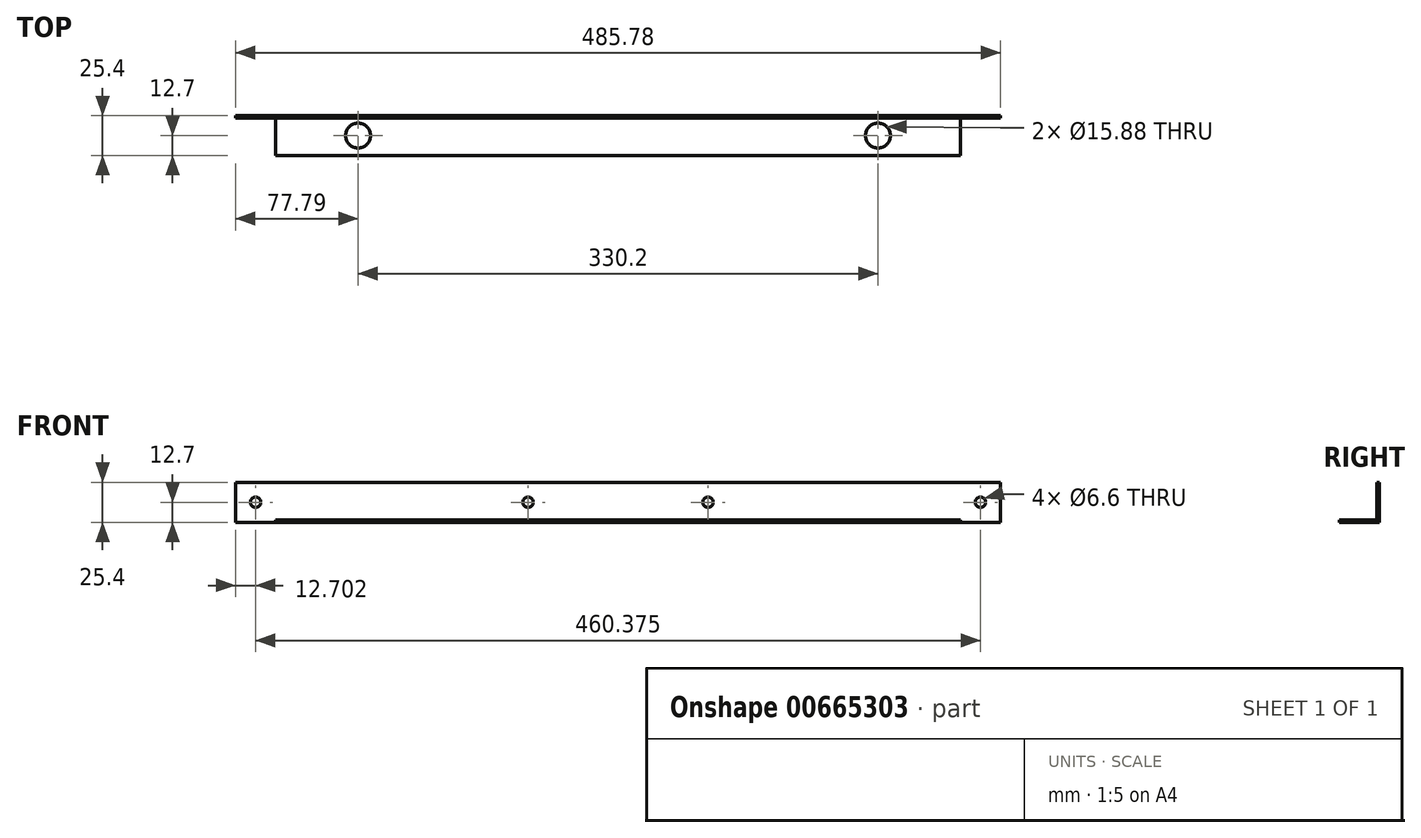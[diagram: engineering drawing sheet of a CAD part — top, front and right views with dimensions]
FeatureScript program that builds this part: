
annotation { "Feature Type Name" : "Feature", "Feature Type Description" : "" }
export const myFeature = defineFeature(function(context is Context, id is Id, definition is map)
    precondition{}
    {
        {
            var Q0;
            Q0=qCreatedBy(makeId("Right.planeOp"),FACE);
            var sketch = newSketch(context, id + "F0", { "sketchPlane" : qUnion([Q0])});
            skLineSegment(sketch, "E0", {"start": v(0, 25.4) * mm, "end": v(0, 0) * mm});
            skLineSegment(sketch, "E1", {"start": v(0, 0) * mm, "end": v(-25.4, 0) * mm});
            skLineSegment(sketch, "E2", {"start": v(-25.4, 0) * mm, "end": v(-25.4, 1.59) * mm});
            skLineSegment(sketch, "E3", {"start": v(-25.4, 1.59) * mm, "end": v(-1.59, 1.59) * mm});
            skLineSegment(sketch, "E4", {"start": v(-1.59, 1.59) * mm, "end": v(-1.59, 25.4) * mm});
            skLineSegment(sketch, "E5", {"start": v(0, 25.4) * mm, "end": v(-1.59, 25.4) * mm});
            skSolve(sketch);
        }
        {
            var Q0;
            Q0=makeQuery(id+"F0.imprint","IMPRINT",FACE,{"disambiguationData":[TD([[makeQuery(id+"F0.imprint","IMPRINT",EDGE,{"derivedFrom":sQuery(id+"F0.wireOp",EDGE,"E0")}),-1.0]])]});
            extrude(context, id + "F1", {"entities" : qUnion([Q0]), "depth" : 485.77 * mm, "offsetDistance" : 25.4 * mm, "symmetric" : true});
        }
        {
            var Q0;
            Q0=makeQuery(id+"F1.opExtrude","SWEPT_FACE",FACE,{"disambiguationData":[OSD([sQuery(id+"F0.wireOp",EDGE,"E1")])]});
            var sketch = newSketch(context, id + "F2", { "sketchPlane" : qUnion([Q0])});
            skCircle(sketch, "E6", {"center": v(-165.1, 12.7) * mm, "radius": 7.94 * mm});
            skCircle(sketch, "E7", {"center": v(165.1, 12.7) * mm, "radius": 7.94 * mm});
            skLineSegment(sketch, "E8", {"start": v(0, 0) * mm, "end": v(0, 25.4) * mm, "construction": true});
            skLineSegment(sketch, "E9", {"start": v(-165.1, 12.7) * mm, "end": v(165.1, 12.7) * mm, "construction": true});
            skPoint(sketch, "E10", {"position": v(0, 12.7) * mm});
            skLineSegment(sketch, "E11.0.0", {"start": v(-242.89, 1.59) * mm, "end": v(-242.89, 25.4) * mm});
            skLineSegment(sketch, "E11.0.1", {"start": v(-242.89, 25.4) * mm, "end": v(242.89, 25.4) * mm});
            skLineSegment(sketch, "E11.0.2", {"start": v(242.89, 25.4) * mm, "end": v(242.89, 1.59) * mm});
            skLineSegment(sketch, "E11.0.3", {"start": v(242.89, 1.59) * mm, "end": v(-242.89, 1.59) * mm});
            skLineSegment(sketch, "E12", {"start": v(-217.49, 1.59) * mm, "end": v(-217.49, 25.4) * mm});
            skLineSegment(sketch, "E13.MirrorCS", {"start": v(217.49, 1.59) * mm, "end": v(217.49, 25.4) * mm});
            skSolve(sketch);
        }
        {
            var Q0;
            Q0=makeQuery(id+"F1.opExtrude","SWEPT_FACE",FACE,{"disambiguationData":[OSD([sQuery(id+"F0.wireOp",EDGE,"E4")])]});
            var sketch = newSketch(context, id + "F3", { "sketchPlane" : qUnion([Q0])});
            skLineSegment(sketch, "E14", {"start": v(0, 0) * mm, "end": v(0, 25.4) * mm, "construction": true});
            skLineSegment(sketch, "E15", {"start": v(230.19, 12.7) * mm, "end": v(-230.19, 12.7) * mm, "construction": true});
            skPoint(sketch, "E15.startSnap0", {"position": v(0, 12.7) * mm});
            skCircle(sketch, "E16", {"center": v(-230.19, 12.7) * mm, "radius": 3.3 * mm});
            skCircle(sketch, "E17", {"center": v(230.19, 12.7) * mm, "radius": 3.3 * mm});
            skLineSegment(sketch, "E18", {"start": v(57.15, 12.7) * mm, "end": v(-57.15, 12.7) * mm, "construction": true});
            skCircle(sketch, "E19", {"center": v(-57.15, 12.7) * mm, "radius": 3.3 * mm});
            skCircle(sketch, "E20", {"center": v(57.15, 12.7) * mm, "radius": 3.3 * mm});
            skSolve(sketch);
        }
        {
            var Q0;
            Q0=makeQuery(id+"F2.imprint","IMPRINT",FACE,{"disambiguationData":[TD([[makeQuery(id+"F2.imprint","IMPRINT",EDGE,{"derivedFrom":sQuery(id+"F2.wireOp",EDGE,"E6")}),1.0]])]});
            var Q1;
            Q1=makeQuery(id+"F2.imprint","IMPRINT",FACE,{"disambiguationData":[TD([[makeQuery(id+"F2.imprint","IMPRINT",EDGE,{"derivedFrom":sQuery(id+"F2.wireOp",EDGE,"E7")}),1.0]])]});
            var Q2;
            {var subQ0=sQuery(id+"F2.wireOp",EDGE,"E11.0.0");Q2=makeQuery(id+"F2.imprint","IMPRINT",FACE,{"disambiguationData":[TD([[makeQuery(id+"F2.imprint","IMPRINT",EDGE,{"derivedFrom":subQ0}),-1.0]])]});}
            var Q3;
            {var subQ0=sQuery(id+"F2.wireOp",EDGE,"E11.0.2");Q3=makeQuery(id+"F2.imprint","IMPRINT",FACE,{"disambiguationData":[TD([[makeQuery(id+"F2.imprint","IMPRINT",EDGE,{"derivedFrom":subQ0}),1.0]])]});}
            extrude(context, id + "F4", {"entities" : qUnion([Q0, Q1, Q2, Q3]), "operationType" : NewBodyOperationType.REMOVE, "oppositeDirection" : true, "depth" : 25.4 * mm, "offsetDistance" : 25.4 * mm});
        }
        {
            var Q0;
            Q0=makeQuery(id+"F3.imprint","IMPRINT",FACE,{"disambiguationData":[TD([[makeQuery(id+"F3.imprint","IMPRINT",EDGE,{"derivedFrom":sQuery(id+"F3.wireOp",EDGE,"E16")}),1.0]])]});
            var Q1;
            Q1=makeQuery(id+"F3.imprint","IMPRINT",FACE,{"disambiguationData":[TD([[makeQuery(id+"F3.imprint","IMPRINT",EDGE,{"derivedFrom":sQuery(id+"F3.wireOp",EDGE,"E17")}),1.0]])]});
            var Q2;
            Q2=makeQuery(id+"F3.imprint","IMPRINT",FACE,{"disambiguationData":[TD([[makeQuery(id+"F3.imprint","IMPRINT",EDGE,{"derivedFrom":sQuery(id+"F3.wireOp",EDGE,"E19")}),1.0]])]});
            var Q3;
            Q3=makeQuery(id+"F3.imprint","IMPRINT",FACE,{"disambiguationData":[TD([[makeQuery(id+"F3.imprint","IMPRINT",EDGE,{"derivedFrom":sQuery(id+"F3.wireOp",EDGE,"E20")}),1.0]])]});
            extrude(context, id + "F5", {"entities" : qUnion([Q0, Q1, Q2, Q3]), "operationType" : NewBodyOperationType.REMOVE, "oppositeDirection" : true, "depth" : 25.4 * mm, "offsetDistance" : 25.4 * mm});
        }
    });
